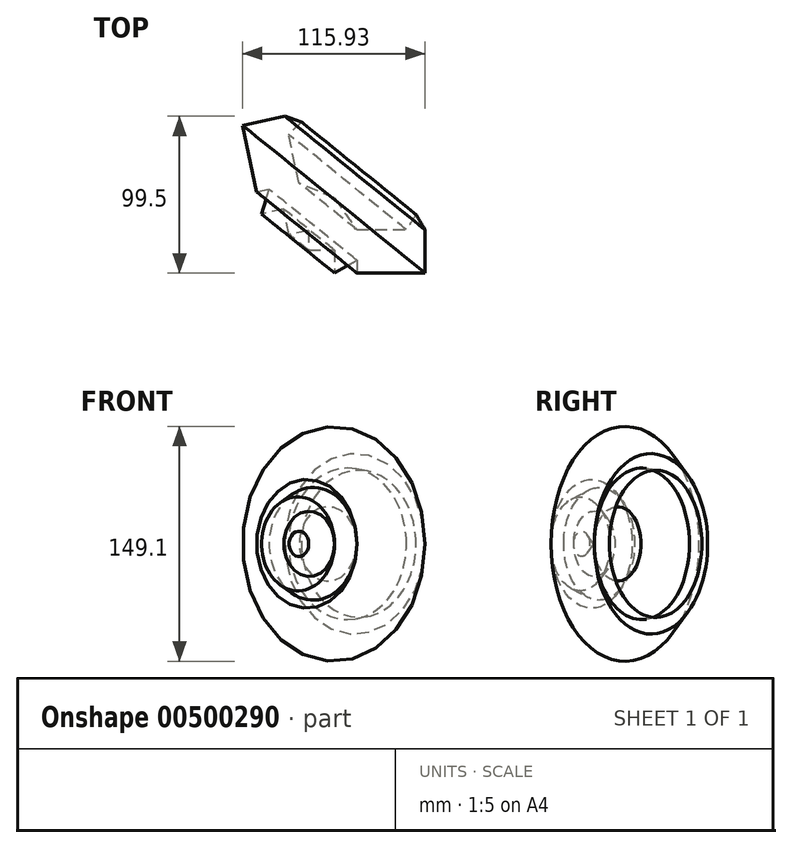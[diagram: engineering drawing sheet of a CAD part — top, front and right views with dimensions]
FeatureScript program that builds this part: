
annotation { "Feature Type Name" : "Feature", "Feature Type Description" : "" }
export const myFeature = defineFeature(function(context is Context, id is Id, definition is map)
    precondition{}
    {
        {
            var Q0;
            Q0=qCreatedBy(makeId("Top.planeOp"),FACE);
            var sketch = newSketch(context, id + "F0", { "sketchPlane" : qUnion([Q0])});
            skLineSegment(sketch, "E0", {"start": v(-57.04, 26.84) * mm, "end": v(-40.4, 47.43) * mm});
            skLineSegment(sketch, "E1", {"start": v(-40.4, 47.43) * mm, "end": v(-26.17, 27.45) * mm});
            skLineSegment(sketch, "E2", {"start": v(-26.17, 27.45) * mm, "end": v(5.32, 27.45) * mm});
            skLineSegment(sketch, "E3", {"start": v(5.32, 27.45) * mm, "end": v(11.37, 37.14) * mm});
            skLineSegment(sketch, "E4", {"start": v(11.37, 37.14) * mm, "end": v(17.13, 27.45) * mm});
            skLineSegment(sketch, "E5", {"start": v(17.13, 27.45) * mm, "end": v(17.13, 0) * mm});
            skLineSegment(sketch, "E6", {"start": v(17.13, 0) * mm, "end": v(-26.17, 0) * mm});
            skLineSegment(sketch, "E7", {"start": v(-26.17, 0) * mm, "end": v(-26.17, 8.07) * mm});
            skLineSegment(sketch, "E8", {"start": v(-26.17, 8.07) * mm, "end": v(-40.4, 0) * mm});
            skLineSegment(sketch, "E9", {"start": v(-40.4, 0) * mm, "end": v(-40.4, 14.43) * mm});
            skLineSegment(sketch, "E10", {"start": v(-40.4, 14.43) * mm, "end": v(-56.74, 14.43) * mm});
            skLineSegment(sketch, "E11", {"start": v(-56.74, 14.43) * mm, "end": v(-57.04, 26.84) * mm});
            skSolve(sketch);
        }
        {
            var Q0;
            Q0=makeQuery(id+"F0.imprint","IMPRINT",FACE,{"disambiguationData":[TD([[makeQuery(id+"F0.imprint","IMPRINT",EDGE,{"derivedFrom":sQuery(id+"F0.wireOp",EDGE,"E0")}),-1.0]])]});
            var Q1;
            Q1=sQuery(id+"F0.wireOp",EDGE,"E0");
            revolve(context, id + "F1", {"entities" : qUnion([Q0]), "axis" : qUnion([Q1]), "revolveType" : RevolveType.FULL});
        }
    });
